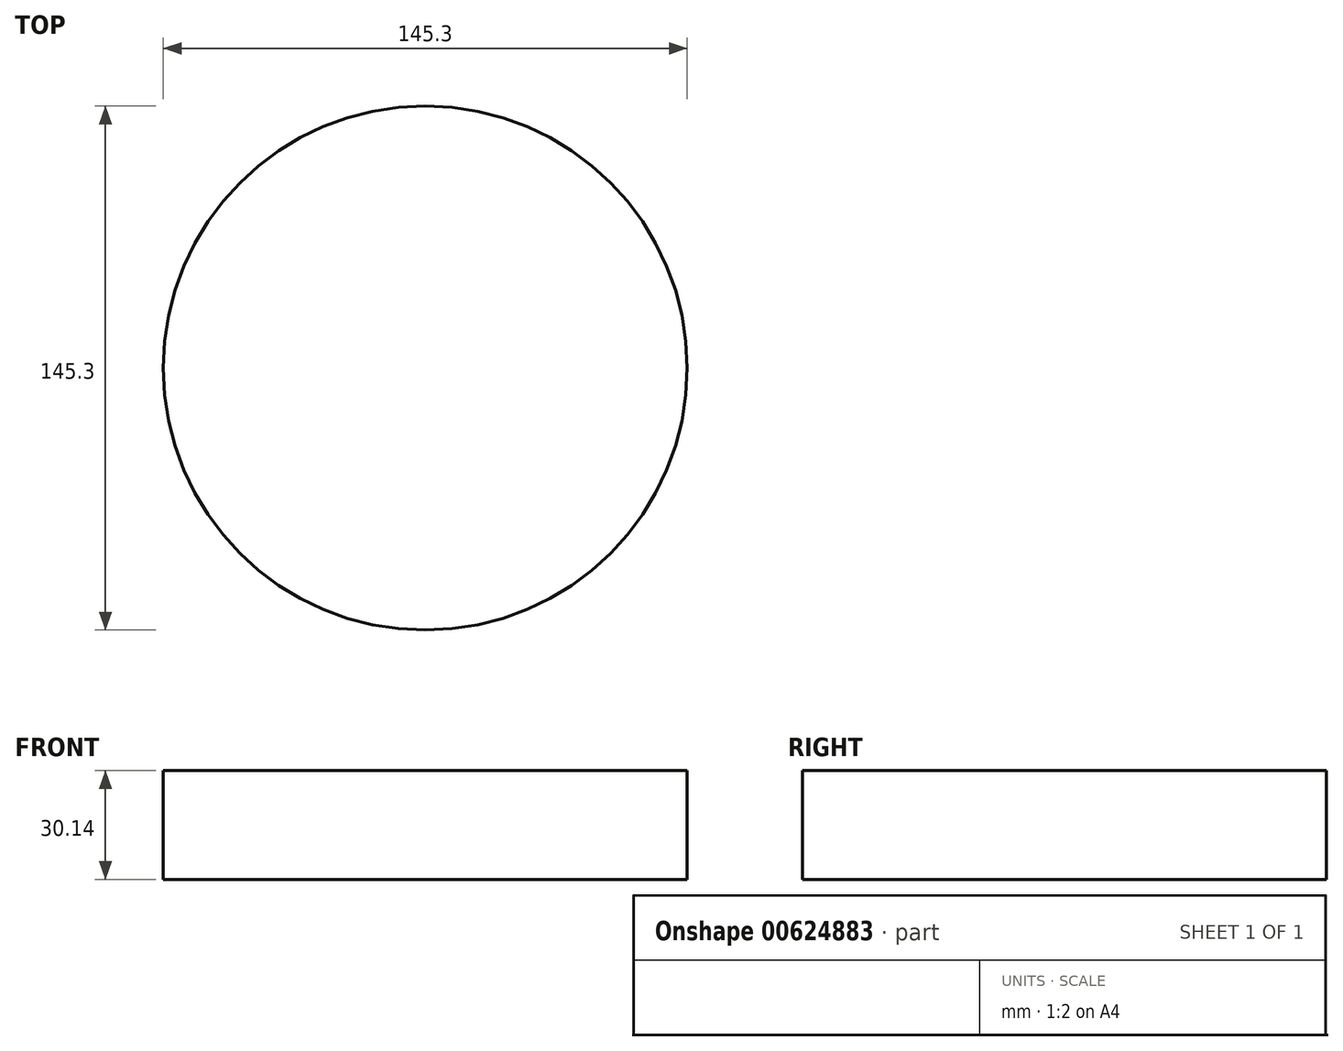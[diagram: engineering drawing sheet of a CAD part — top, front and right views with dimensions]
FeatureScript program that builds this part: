
annotation { "Feature Type Name" : "Feature", "Feature Type Description" : "" }
export const myFeature = defineFeature(function(context is Context, id is Id, definition is map)
    precondition{}
    {
        {
            var Q0;
            Q0=qCreatedBy(makeId("Front.planeOp"),FACE);
            var sketch = newSketch(context, id + "F0", { "sketchPlane" : qUnion([Q0])});
            skLineSegment(sketch, "E0.bottom", {"start": v(-48.05, 34.47) * mm, "end": v(24.6, 34.47) * mm});
            skLineSegment(sketch, "E0.top", {"start": v(-48.05, 4.33) * mm, "end": v(24.6, 4.33) * mm});
            skLineSegment(sketch, "E0.left", {"start": v(-48.05, 34.47) * mm, "end": v(-48.05, 4.33) * mm});
            skLineSegment(sketch, "E0.right", {"start": v(24.6, 34.47) * mm, "end": v(24.6, 4.33) * mm});
            skSolve(sketch);
        }
        {
            var Q0;
            Q0 = qSketchRegion(id + "F0", true);
            var Q1;
            Q1=sQuery(id+"F0.wireOp",EDGE,"E0.left");
            revolve(context, id + "F1", {"entities" : qUnion([Q0]), "axis" : qUnion([Q1]), "revolveType" : RevolveType.FULL});
        }
        {
            var Q0;
            Q0=makeQuery(id+"F1.opRevolve","SWEPT_FACE",FACE,{"disambiguationData":[OSD([sQuery(id+"F0.wireOp",EDGE,"E0.bottom")])]});
            var sketch = newSketch(context, id + "F2", { "sketchPlane" : qUnion([Q0])});
            skCircle(sketch, "E1", {"center": v(-77.07, -12.2) * mm, "radius": 15.1 * mm});
            skLineSegment(sketch, "E2", {"start": v(-92.31, 35.67) * mm, "end": v(-19.71, -5.8) * mm});
            skSolve(sketch);
        }
        {
            var Q0;
            Q0=sQuery(id+"F2.wireOp",EDGE,"E1");
            var Q1;
            Q1=sQuery(id+"F2.wireOp",EDGE,"E2");
            revolve(context, id + "F3", {"bodyType" : ToolBodyType.SURFACE, "surfaceEntities" : qUnion([Q0]), "axis" : qUnion([Q1]), "revolveType" : RevolveType.ONE_DIRECTION, "oppositeDirection" : true, "angle" : 180 * degree});
        }
    });
